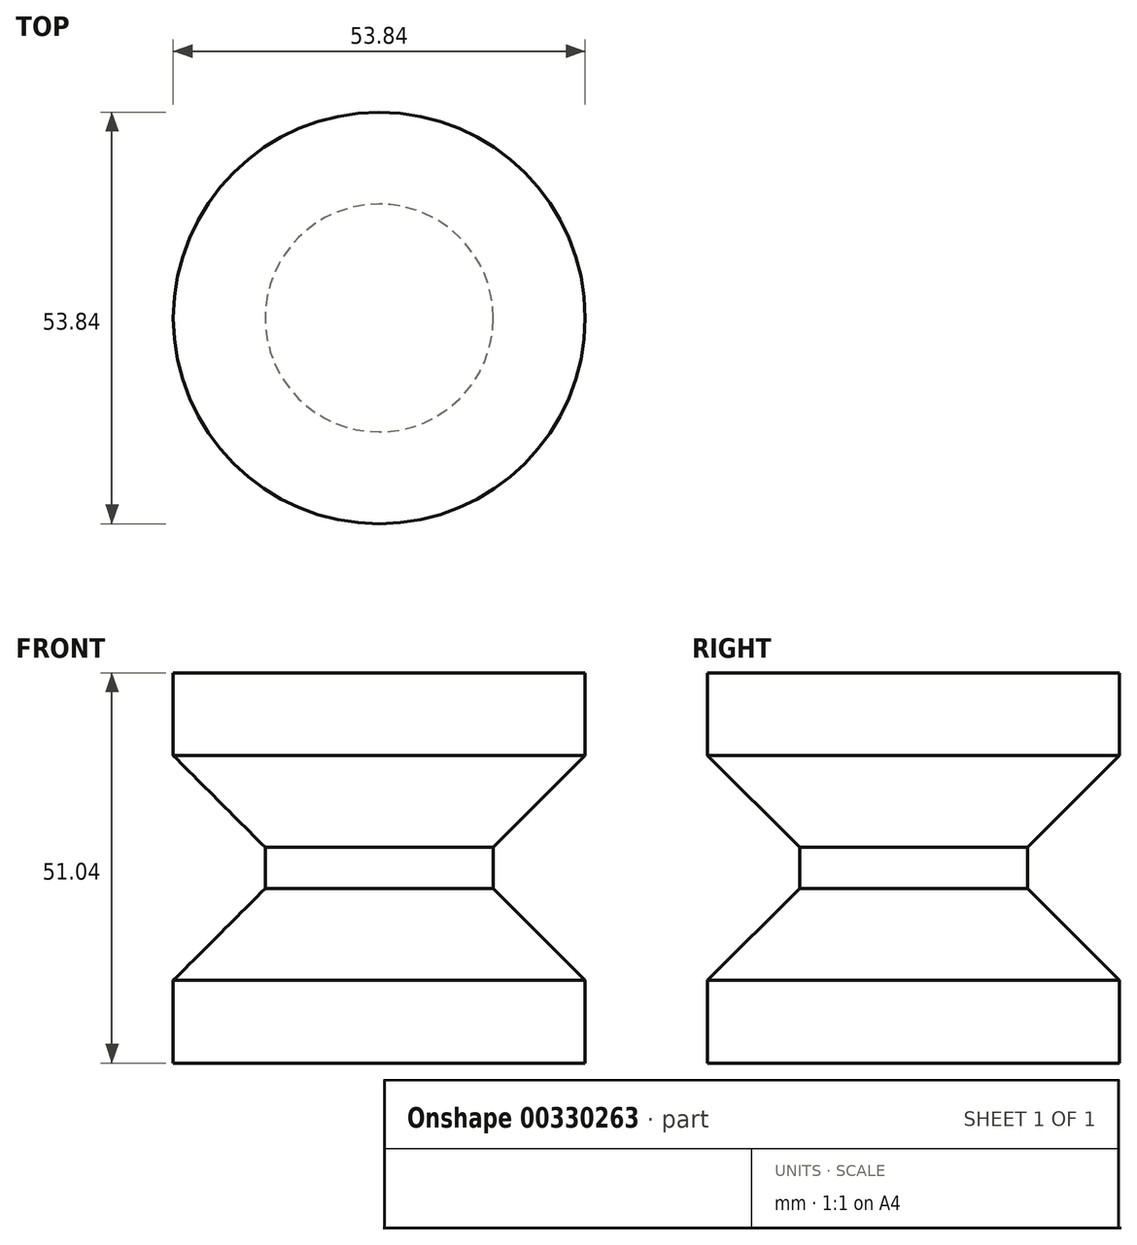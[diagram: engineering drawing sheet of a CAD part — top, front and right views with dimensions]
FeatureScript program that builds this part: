
annotation { "Feature Type Name" : "Feature", "Feature Type Description" : "" }
export const myFeature = defineFeature(function(context is Context, id is Id, definition is map)
    precondition{}
    {
        {
            var Q0;
            Q0=qCreatedBy(makeId("Front.planeOp"),FACE);
            var sketch = newSketch(context, id + "F0", { "sketchPlane" : qUnion([Q0])});
            skLineSegment(sketch, "E0", {"start": v(0, 33.46) * mm, "end": v(-26.92, 33.46) * mm});
            skLineSegment(sketch, "E1", {"start": v(-26.92, 22.65) * mm, "end": v(-14.9, 10.63) * mm});
            skLineSegment(sketch, "E2", {"start": v(-14.9, 10.63) * mm, "end": v(-14.9, 5.25) * mm});
            skLineSegment(sketch, "E3", {"start": v(-14.9, 5.25) * mm, "end": v(-26.92, -6.77) * mm});
            skLineSegment(sketch, "E4", {"start": v(-26.92, -6.77) * mm, "end": v(-26.92, -17.58) * mm});
            skLineSegment(sketch, "E5", {"start": v(-26.92, -17.58) * mm, "end": v(0, -17.58) * mm});
            skLineSegment(sketch, "E6", {"start": v(0, -17.58) * mm, "end": v(0, 33.46) * mm});
            skLineSegment(sketch, "E7", {"start": v(-26.92, 33.46) * mm, "end": v(-26.92, 22.65) * mm});
            skSolve(sketch);
        }
        {
            var Q0;
            Q0 = qSketchRegion(id + "F0", true);
            var Q1;
            Q1=sQuery(id+"F0.wireOp",EDGE,"E6");
            revolve(context, id + "F1", {"entities" : qUnion([Q0]), "axis" : qUnion([Q1]), "revolveType" : RevolveType.FULL});
        }
    });
